# Revit family: +_
name_source: partatom
category: Plumbing Fixtures
units: mm (PartAtom-declared; Revit-internal decimal feet)

## family parameters
Always vertical = No
Cut with Voids When Loaded = No
OmniClass Number = 23.31.17.00
OmniClass Title = Showers
Part Type = Normal
Room Calculation Point = No
Round Connector Dimension = Use Diameter
Shared = No
Work Plane-Based = Yes

## types (4) — shared parameters
Default Elevation = 1219 mm
Description = AXOR ShowerComposition Thermostatic module 610/110 for concealed installation for 4 functions
Manufacturer = AXOR
Model = 12573CHN
Product Guid = 27faf866-2fb1-42b1-900d-c20c588428ec
Product Page URL = https://www.axor-design.com
Product data url = https://bimobject.com
URL = https://www.axor-design.com
Version = 1
zero-valued in all types: Edition number

## per-type parameters (varying)
| type | Material 1 |
| 007 Chrome | AXOR - Metal - 007 Chrome |
| 347 Brushed Black Chrome | AXOR - Metal - 347 Brushed Black Chrome |
| 677 Matte Black | AXOR - Metal - 677 Matte Black |
| 997 Polished Gold Optic | AXOR - Metal - 997 Polished Gold Optic |

## geometry (parser evidence)
native form markers: Sweep x1
no freeform markers — native parametric forms only
